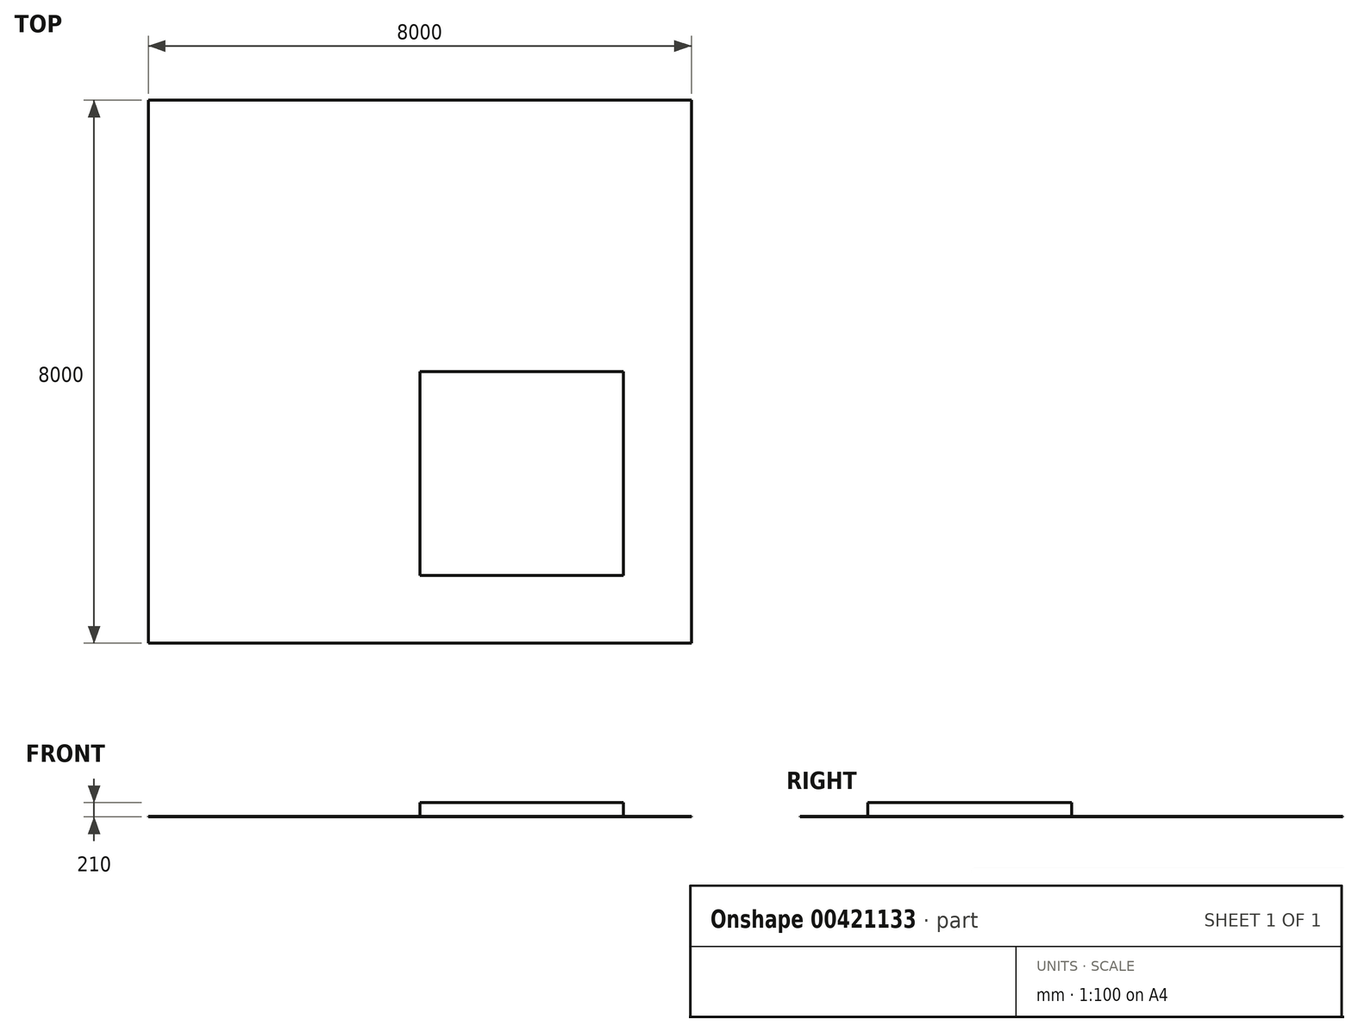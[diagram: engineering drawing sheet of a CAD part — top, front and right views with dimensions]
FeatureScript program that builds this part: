
annotation { "Feature Type Name" : "Feature", "Feature Type Description" : "" }
export const myFeature = defineFeature(function(context is Context, id is Id, definition is map)
    precondition{}
    {
        {
            var Q0;
            Q0=qCreatedBy(makeId("Top.planeOp"),FACE);
            var sketch = newSketch(context, id + "F0", { "sketchPlane" : qUnion([Q0])});
            skLineSegment(sketch, "E0.bottom", {"start": v(4000, -4000) * mm, "end": v(-4000, -4000) * mm});
            skLineSegment(sketch, "E0.top", {"start": v(4000, 4000) * mm, "end": v(-4000, 4000) * mm});
            skLineSegment(sketch, "E0.left", {"start": v(4000, -4000) * mm, "end": v(4000, 4000) * mm});
            skLineSegment(sketch, "E0.right", {"start": v(-4000, -4000) * mm, "end": v(-4000, 4000) * mm});
            skPoint(sketch, "E0.middle", {"position": v(0, 0) * mm});
            skSolve(sketch);
        }
        {
            var Q0;
            Q0 = qSketchRegion(id + "F0", true);
            extrude(context, id + "F1", {"entities" : qUnion([Q0]), "oppositeDirection" : true, "depth" : 10 * mm});
        }
        {
            var Q0;
            Q0=makeQuery(id+"F1.opExtrude","CAP_FACE",FACE,{"disambiguationData":[OSD([sQuery(id+"F0.wireOp",EDGE,"E0.bottom"),sQuery(id+"F0.wireOp",EDGE,"E0.top"),sQuery(id+"F0.wireOp",EDGE,"E0.left"),sQuery(id+"F0.wireOp",EDGE,"E0.right")])],"isStart":true});
            var sketch = newSketch(context, id + "F2", { "sketchPlane" : qUnion([Q0])});
            skLineSegment(sketch, "E1.bottom", {"start": v(0, 0) * mm, "end": v(3000, 0) * mm});
            skLineSegment(sketch, "E1.top", {"start": v(0, -3000) * mm, "end": v(3000, -3000) * mm});
            skLineSegment(sketch, "E1.left", {"start": v(0, 0) * mm, "end": v(0, -3000) * mm});
            skLineSegment(sketch, "E1.right", {"start": v(3000, 0) * mm, "end": v(3000, -3000) * mm});
            skSolve(sketch);
        }
        {
            var Q0;
            Q0 = qSketchRegion(id + "F2", true);
            extrude(context, id + "F3", {"entities" : qUnion([Q0]), "depth" : 200 * mm});
        }
    });
